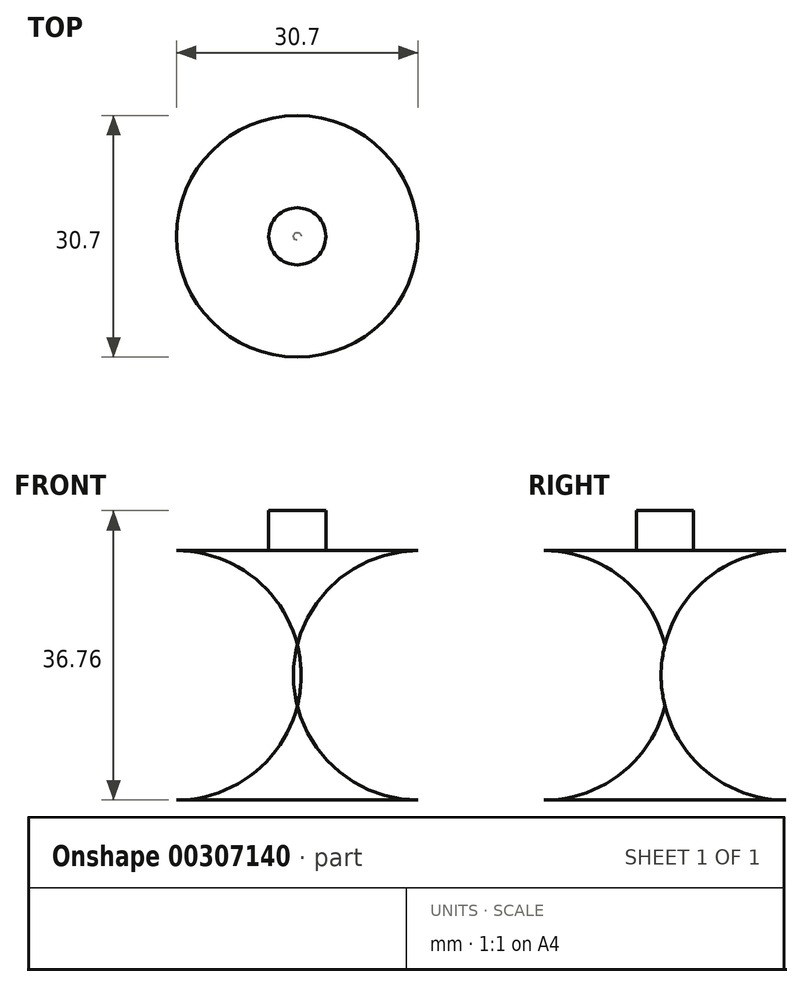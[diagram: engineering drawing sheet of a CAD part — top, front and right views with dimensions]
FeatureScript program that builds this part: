
annotation { "Feature Type Name" : "Feature", "Feature Type Description" : "" }
export const myFeature = defineFeature(function(context is Context, id is Id, definition is map)
    precondition{}
    {
        {
            var Q0;
            Q0=qCreatedBy(makeId("Front.planeOp"),FACE);
            var sketch = newSketch(context, id + "F0", { "sketchPlane" : qUnion([Q0])});
            skLineSegment(sketch, "E0", {"start": v(0, 0) * mm, "end": v(15.35, 0) * mm});
            skArc(sketch, "E1", {"start": v(15.35, 0) * mm, "mid": v(31.2, 15.84) * mm, "end": v(15.35, 31.68) * mm});
            skLineSegment(sketch, "E2", {"start": v(15.35, 31.68) * mm, "end": v(0, 31.68) * mm});
            skLineSegment(sketch, "E3", {"start": v(0, 31.68) * mm, "end": v(0, 0) * mm});
            skSolve(sketch);
        }
        {
            var Q0;
            Q0 = qSketchRegion(id + "F0", true);
            var Q1;
            Q1=sQuery(id+"F0.wireOp",EDGE,"E3");
            revolve(context, id + "F1", {"entities" : qUnion([Q0]), "axis" : qUnion([Q1]), "revolveType" : RevolveType.FULL});
        }
        {
            var Q0;
            Q0=makeQuery(id+"F1.opRevolve","SWEPT_FACE",FACE,{"disambiguationData":[OSD([sQuery(id+"F0.wireOp",EDGE,"E2")])]});
            var sketch = newSketch(context, id + "F2", { "sketchPlane" : qUnion([Q0])});
            skCircle(sketch, "E4", {"center": v(0, 0) * mm, "radius": 3.62 * mm});
            skSolve(sketch);
        }
        {
            var Q0;
            Q0 = qSketchRegion(id + "F2", true);
            extrude(context, id + "F3", {"entities" : qUnion([Q0]), "operationType" : NewBodyOperationType.ADD, "depth" : 5.08 * mm});
        }
        {
            var Q0;
            Q0=qCreatedBy(makeId("Front.planeOp"),FACE);
            var sketch = newSketch(context, id + "F4", { "sketchPlane" : qUnion([Q0])});
            skLineSegment(sketch, "E5", {"start": v(-7.32, 22.3) * mm, "end": v(-18.84, 23.5) * mm});
            skLineSegment(sketch, "E6", {"start": v(-18.84, 23.5) * mm, "end": v(-13.11, 17.77) * mm});
            skLineSegment(sketch, "E7", {"start": v(-13.11, 17.77) * mm, "end": v(-7.32, 22.3) * mm});
            skLineSegment(sketch, "E8", {"start": v(4.75, 21.89) * mm, "end": v(14.51, 23.14) * mm});
            skLineSegment(sketch, "E9", {"start": v(14.51, 23.14) * mm, "end": v(10.47, 17.35) * mm});
            skLineSegment(sketch, "E10", {"start": v(10.47, 17.35) * mm, "end": v(4.75, 21.89) * mm});
            skLineSegment(sketch, "E11", {"start": v(-10.11, 11.14) * mm, "end": v(-5.65, 10.23) * mm});
            skLineSegment(sketch, "E12", {"start": v(-5.65, 10.23) * mm, "end": v(-5.65, 7.58) * mm});
            skLineSegment(sketch, "E13", {"start": v(-5.65, 7.58) * mm, "end": v(-3, 7.58) * mm});
            skLineSegment(sketch, "E14", {"start": v(-3, 7.58) * mm, "end": v(-3, 10.23) * mm});
            skLineSegment(sketch, "E15", {"start": v(-3, 10.23) * mm, "end": v(7.19, 10.23) * mm});
            skLineSegment(sketch, "E16", {"start": v(7.19, 10.23) * mm, "end": v(9.5, 10.86) * mm});
            skLineSegment(sketch, "E17", {"start": v(9.5, 10.86) * mm, "end": v(8.37, 8.21) * mm});
            skLineSegment(sketch, "E18", {"start": v(8.37, 8.21) * mm, "end": v(4.75, 6.4) * mm});
            skLineSegment(sketch, "E19", {"start": v(4.75, 6.4) * mm, "end": v(1.54, 6.4) * mm});
            skLineSegment(sketch, "E20", {"start": v(1.54, 6.4) * mm, "end": v(-3.2, 6.4) * mm});
            skLineSegment(sketch, "E21", {"start": v(-3.2, 6.4) * mm, "end": v(-7.25, 6.4) * mm});
            skLineSegment(sketch, "E22", {"start": v(-7.25, 6.4) * mm, "end": v(-10.25, 8.21) * mm});
            skLineSegment(sketch, "E23", {"start": v(-10.25, 8.21) * mm, "end": v(-11.51, 11.63) * mm});
            skLineSegment(sketch, "E24", {"start": v(-11.51, 11.63) * mm, "end": v(-10.11, 11.14) * mm});
            skSolve(sketch);
        }
        {
            var Q0;
            Q0 = qSketchRegion(id + "F4", true);
            extrude(context, id + "F5", {"entities" : qUnion([Q0]), "operationType" : NewBodyOperationType.REMOVE, "oppositeDirection" : true, "depth" : 50.8 * mm});
        }
    });
